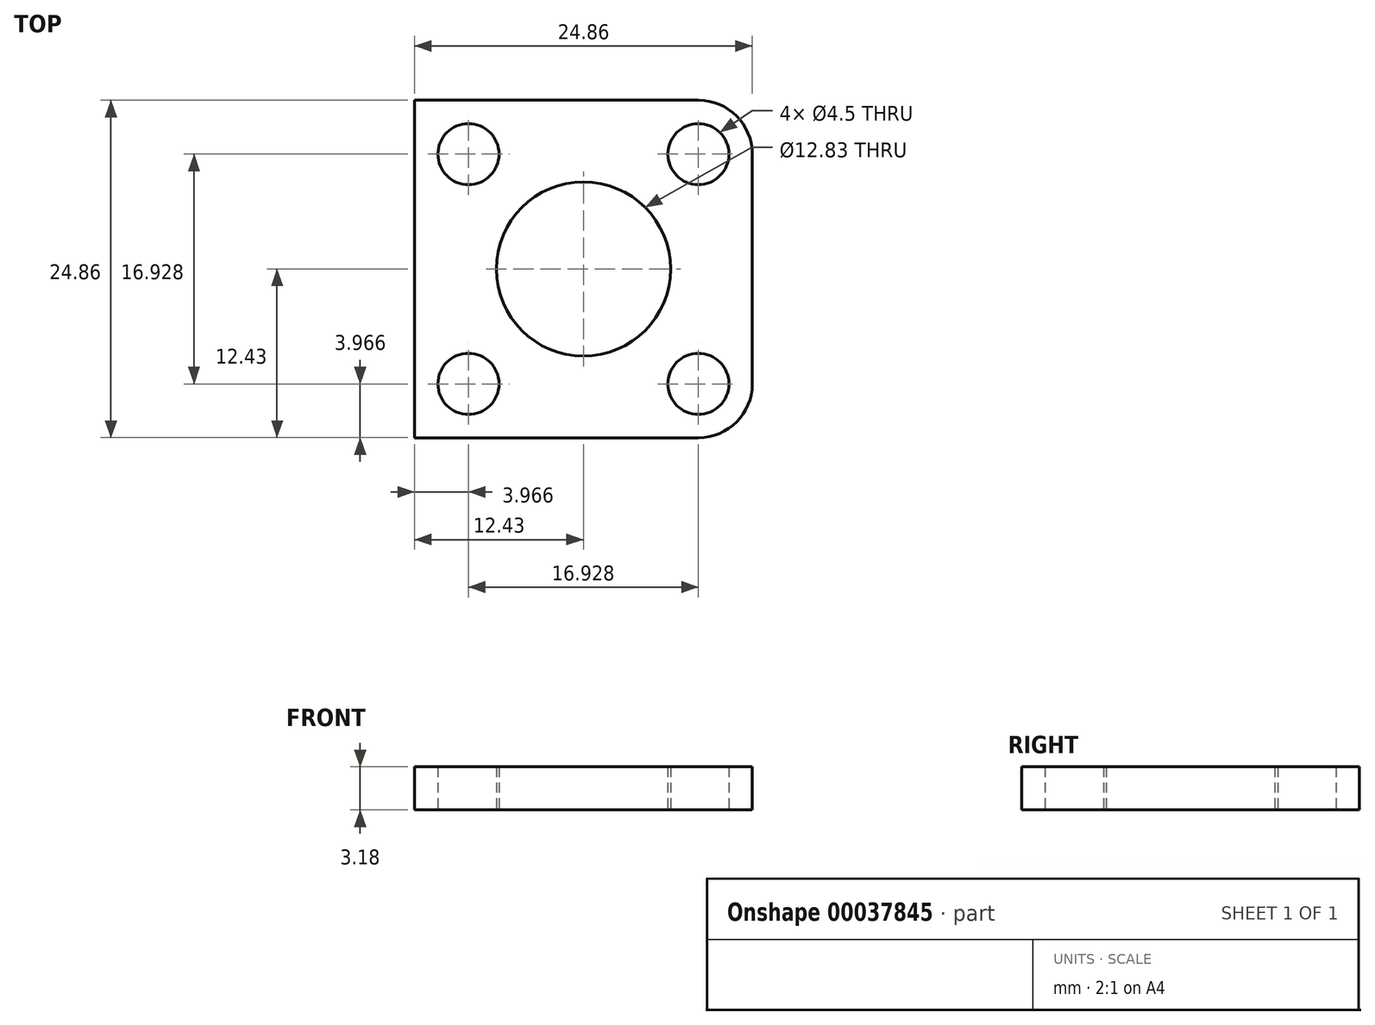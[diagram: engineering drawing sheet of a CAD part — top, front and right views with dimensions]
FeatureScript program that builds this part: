
annotation { "Feature Type Name" : "Feature", "Feature Type Description" : "" }
export const myFeature = defineFeature(function(context is Context, id is Id, definition is map)
    precondition{}
    {
        {
            var Q0;
            Q0=qCreatedBy(makeId("Top.planeOp"),FACE);
            var sketch = newSketch(context, id + "F0", { "sketchPlane" : qUnion([Q0])});
            skLineSegment(sketch, "E0.rect.bottom", {"start": v(12.43, 12.43) * mm, "end": v(-12.43, 12.43) * mm});
            skLineSegment(sketch, "E0.rect.top", {"start": v(12.43, -12.43) * mm, "end": v(-12.43, -12.43) * mm});
            skLineSegment(sketch, "E0.rect.left", {"start": v(12.43, 12.43) * mm, "end": v(12.43, -12.43) * mm});
            skLineSegment(sketch, "E0.rect.right", {"start": v(-12.43, 12.43) * mm, "end": v(-12.43, -12.43) * mm});
            skPoint(sketch, "E0.rect.middle", {"position": v(0, 0) * mm});
            skLineSegment(sketch, "E1.rect.bottom", {"start": v(8.46, 8.46) * mm, "end": v(-8.46, 8.46) * mm, "construction": true});
            skLineSegment(sketch, "E1.rect.top", {"start": v(8.46, -8.46) * mm, "end": v(-8.46, -8.46) * mm, "construction": true});
            skLineSegment(sketch, "E1.rect.left", {"start": v(8.46, 8.46) * mm, "end": v(8.46, -8.46) * mm, "construction": true});
            skLineSegment(sketch, "E1.rect.right", {"start": v(-8.46, 8.46) * mm, "end": v(-8.46, -8.46) * mm, "construction": true});
            skCircle(sketch, "E2", {"center": v(8.46, 8.46) * mm, "radius": 3.97 * mm, "construction": true});
            skCircle(sketch, "E3", {"center": v(-8.46, 8.46) * mm, "radius": 2.25 * mm});
            skCircle(sketch, "E4", {"center": v(8.46, 8.46) * mm, "radius": 2.25 * mm});
            skCircle(sketch, "E5", {"center": v(-8.46, -8.46) * mm, "radius": 2.25 * mm});
            skCircle(sketch, "E6", {"center": v(8.46, -8.46) * mm, "radius": 2.25 * mm});
            skCircle(sketch, "E7", {"center": v(0, 0) * mm, "radius": 6.41 * mm});
            skSolve(sketch);
        }
        {
            var Q0;
            Q0=qSketchRegion(id+"F0",true);
            extrude(context, id + "F1", {"entities" : qUnion([Q0]), "depth" : 3.17 * mm});
        }
        {
            var Q0;
            Q0=makeQuery(id+"F1.opExtrude","SWEPT_EDGE",EDGE,{"disambiguationData":[OSD([sQuery(id+"F0.wireOp",EDGE,"E0.rect.top"),sQuery(id+"F0.wireOp",EDGE,"E0.rect.left")])]});
            var Q1;
            Q1=makeQuery(id+"F1.opExtrude","SWEPT_EDGE",EDGE,{"disambiguationData":[OSD([sQuery(id+"F0.wireOp",EDGE,"E0.rect.bottom"),sQuery(id+"F0.wireOp",EDGE,"E0.rect.left")])]});
            fillet(context, id + "F2", {"entities" : qUnion([Q0, Q1]), "radius" : 3.97 * mm, "tangentPropagation" : true, "allowEdgeOverflow" : false});
        }
    });
